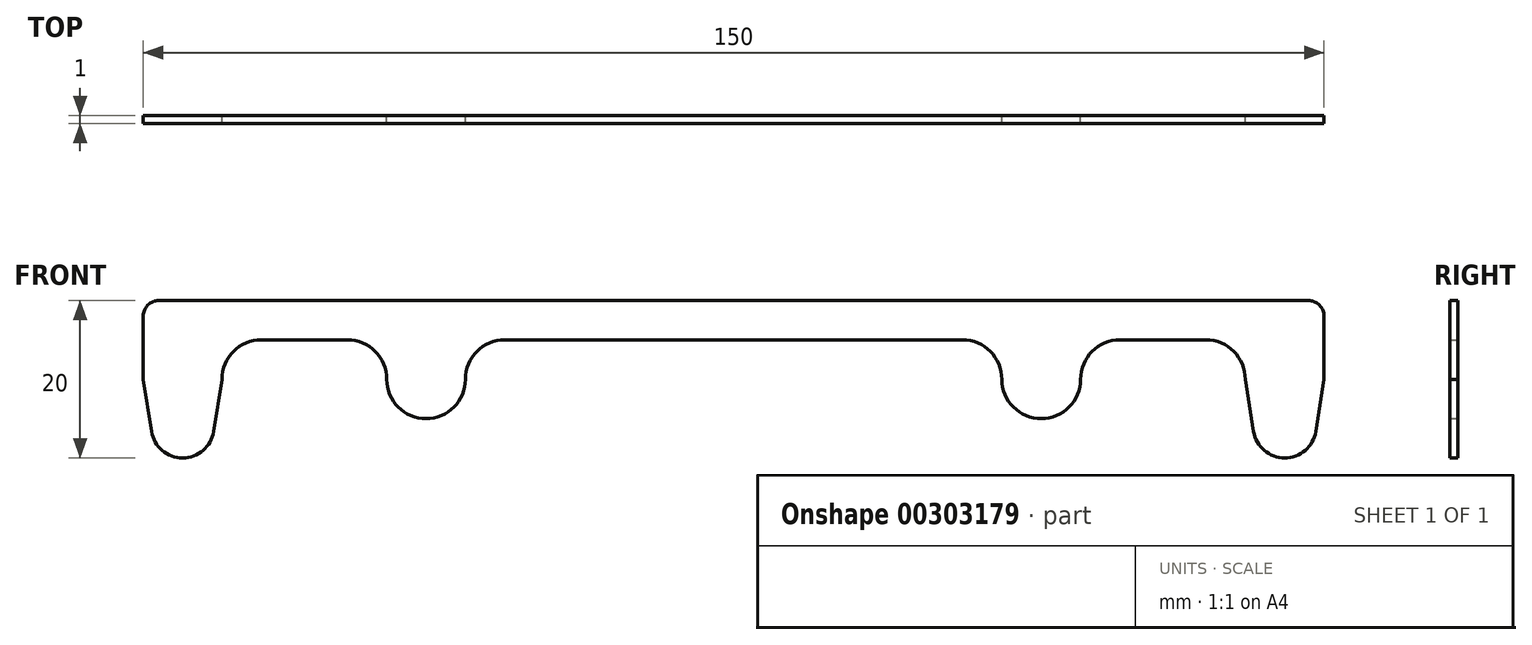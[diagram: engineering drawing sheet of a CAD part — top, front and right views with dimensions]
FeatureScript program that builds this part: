
annotation { "Feature Type Name" : "Feature", "Feature Type Description" : "" }
export const myFeature = defineFeature(function(context is Context, id is Id, definition is map)
    precondition{}
    {
        {
            var Q0;
            Q0=qCreatedBy(makeId("Front.planeOp"),FACE);
            var sketch = newSketch(context, id + "F0", { "sketchPlane" : qUnion([Q0])});
            skLineSegment(sketch, "E0.top", {"start": v(-28.13, 20.35) * mm, "end": v(29.87, 20.35) * mm});
            skLineSegment(sketch, "E0.left", {"start": v(-30.13, 10.35) * mm, "end": v(-30.13, 18.35) * mm});
            skLineSegment(sketch, "E1", {"start": v(27.87, 15.35) * mm, "end": v(15.8, 15.35) * mm});
            skLineSegment(sketch, "E2.top", {"start": v(-3.28, 5.35) * mm, "end": v(-3.28, 5.35) * mm});
            skLineSegment(sketch, "E2.left", {"start": v(-8.28, 10.35) * mm, "end": v(-8.28, 10.35) * mm});
            skLineSegment(sketch, "E2.right", {"start": v(1.72, 10.35) * mm, "end": v(1.72, 10.35) * mm});
            skLineSegment(sketch, "E3.trimOffspring", {"start": v(-13.28, 15.35) * mm, "end": v(-15.13, 15.35) * mm});
            skPoint(sketch, "E4.visualSharp", {"position": v(-20.13, 15.35) * mm});
            skArc(sketch, "E4.filletArc", {"start": v(-15.13, 15.35) * mm, "mid": v(-18.67, 13.89) * mm, "end": v(-20.13, 10.35) * mm});
            skPoint(sketch, "E5.visualSharp", {"position": v(-8.28, 15.35) * mm});
            skPoint(sketch, "E6.visualSharp", {"position": v(-8.28, 5.35) * mm});
            skPoint(sketch, "E7.visualSharp", {"position": v(1.72, 5.35) * mm});
            skPoint(sketch, "E8.visualSharp", {"position": v(1.72, 15.35) * mm});
            skPoint(sketch, "E9.visualSharp", {"position": v(-20.13, 0.35) * mm});
            skPoint(sketch, "E10.visualSharp", {"position": v(-30.13, 0.35) * mm});
            skPoint(sketch, "E11.visualSharp", {"position": v(-30.13, 20.35) * mm});
            skArc(sketch, "E11.filletArc", {"start": v(-28.13, 20.35) * mm, "mid": v(-29.54, 19.76) * mm, "end": v(-30.13, 18.35) * mm});
            skLineSegment(sketch, "E12", {"start": v(44.87, 39.66) * mm, "end": v(44.87, -4.16) * mm, "construction": true});
            skLineSegment(sketch, "E13.top", {"start": v(5.8, 5.35) * mm, "end": v(5.8, 5.35) * mm});
            skLineSegment(sketch, "E13.left", {"start": v(10.8, 10.35) * mm, "end": v(10.8, 10.35) * mm});
            skLineSegment(sketch, "E13.right", {"start": v(0.8, 10.35) * mm, "end": v(0.8, 10.35) * mm});
            skLineSegment(sketch, "E14", {"start": v(-13.28, 15.35) * mm, "end": v(-4.2, 15.35) * mm});
            skPoint(sketch, "E15.visualSharp", {"position": v(0.8, 15.35) * mm});
            skArc(sketch, "E15.filletArc", {"start": v(0.8, 10.35) * mm, "mid": v(-0.67, 13.89) * mm, "end": v(-4.2, 15.35) * mm});
            skPoint(sketch, "E16.newPointB", {"position": v(6.72, 15.35) * mm});
            skArc(sketch, "E16.filletArc", {"start": v(15.8, 15.35) * mm, "mid": v(12.26, 13.89) * mm, "end": v(10.8, 10.35) * mm});
            skPoint(sketch, "E17.visualSharp", {"position": v(10.8, 5.35) * mm});
            skArc(sketch, "E17.filletArc", {"start": v(5.8, 5.35) * mm, "mid": v(9.33, 6.81) * mm, "end": v(10.8, 10.35) * mm});
            skPoint(sketch, "E18.visualSharp", {"position": v(0.8, 5.35) * mm});
            skArc(sketch, "E18.filletArc", {"start": v(0.8, 10.35) * mm, "mid": v(2.26, 6.81) * mm, "end": v(5.8, 5.35) * mm});
            skLineSegment(sketch, "E19.MirrorCS", {"start": v(103.02, 15.35) * mm, "end": v(104.87, 15.35) * mm});
            skArc(sketch, "E20.MirrorCS", {"start": v(117.87, 20.35) * mm, "mid": v(119.28, 19.76) * mm, "end": v(119.87, 18.35) * mm});
            skArc(sketch, "E21.MirrorCS", {"start": v(88.94, 10.35) * mm, "mid": v(87.48, 6.81) * mm, "end": v(83.94, 5.35) * mm});
            skArc(sketch, "E22.MirrorCS", {"start": v(104.87, 15.35) * mm, "mid": v(108.4, 13.89) * mm, "end": v(109.87, 10.35) * mm});
            skLineSegment(sketch, "E23.MirrorCS", {"start": v(103.02, 15.35) * mm, "end": v(93.94, 15.35) * mm});
            skArc(sketch, "E24.MirrorCS", {"start": v(88.94, 10.35) * mm, "mid": v(90.4, 13.89) * mm, "end": v(93.94, 15.35) * mm});
            skArc(sketch, "E25.MirrorCS", {"start": v(83.94, 5.35) * mm, "mid": v(80.4, 6.81) * mm, "end": v(78.94, 10.35) * mm});
            skPoint(sketch, "E26.MirrorP", {"position": v(88.94, 5.35) * mm});
            skLineSegment(sketch, "E27.MirrorCS", {"start": v(117.87, 20.35) * mm, "end": v(59.87, 20.35) * mm});
            skLineSegment(sketch, "E28.MirrorCS", {"start": v(78.94, 10.35) * mm, "end": v(78.94, 10.35) * mm});
            skPoint(sketch, "E29.MirrorP", {"position": v(88.02, 15.35) * mm});
            skPoint(sketch, "E30.MirrorP", {"position": v(98.02, 15.35) * mm});
            skPoint(sketch, "E31.MirrorP", {"position": v(109.87, 15.35) * mm});
            skLineSegment(sketch, "E32.MirrorCS", {"start": v(93.02, 5.35) * mm, "end": v(93.02, 5.35) * mm});
            skLineSegment(sketch, "E33.MirrorCS", {"start": v(119.87, 10.35) * mm, "end": v(119.87, 18.35) * mm});
            skArc(sketch, "E34.MirrorCS", {"start": v(73.94, 15.35) * mm, "mid": v(77.48, 13.89) * mm, "end": v(78.94, 10.35) * mm});
            skLineSegment(sketch, "E35.MirrorCS", {"start": v(61.87, 15.35) * mm, "end": v(73.94, 15.35) * mm});
            skPoint(sketch, "E36.MirrorP", {"position": v(109.87, 0.35) * mm});
            skLineSegment(sketch, "E37.MirrorCS", {"start": v(88.02, 10.35) * mm, "end": v(88.02, 10.35) * mm});
            skPoint(sketch, "E38.MirrorP", {"position": v(98.02, 5.35) * mm});
            skLineSegment(sketch, "E39.MirrorCS", {"start": v(88.94, 10.35) * mm, "end": v(88.94, 10.35) * mm});
            skPoint(sketch, "E40.MirrorP", {"position": v(119.87, 20.35) * mm});
            skPoint(sketch, "E41.MirrorP", {"position": v(78.94, 5.35) * mm});
            skPoint(sketch, "E42.MirrorP", {"position": v(119.87, 0.35) * mm});
            skPoint(sketch, "E43.MirrorP", {"position": v(88.94, 15.35) * mm});
            skLineSegment(sketch, "E44.MirrorCS", {"start": v(98.02, 10.35) * mm, "end": v(98.02, 10.35) * mm});
            skPoint(sketch, "E45.MirrorP", {"position": v(88.02, 5.35) * mm});
            skLineSegment(sketch, "E46.MirrorCS", {"start": v(83.94, 5.35) * mm, "end": v(83.94, 5.35) * mm});
            skPoint(sketch, "E47.MirrorP", {"position": v(83.02, 15.35) * mm});
            skLineSegment(sketch, "E48", {"start": v(29.87, 20.35) * mm, "end": v(59.87, 20.35) * mm});
            skPoint(sketch, "E0.right.start.orphan", {"position": v(29.87, 17.35) * mm});
            skPoint(sketch, "E49.MirrorCS.end.orphan", {"position": v(59.87, 17.35) * mm});
            skLineSegment(sketch, "E50", {"start": v(27.87, 15.35) * mm, "end": v(61.87, 15.35) * mm});
            skArc(sketch, "E51", {"start": v(-29.08, 3.72) * mm, "mid": v(-25.13, 0.35) * mm, "end": v(-21.18, 3.72) * mm});
            skLineSegment(sketch, "E52", {"start": v(-20.13, 10.35) * mm, "end": v(-21.18, 3.72) * mm});
            skLineSegment(sketch, "E53", {"start": v(-25.13, 4.35) * mm, "end": v(-25.13, 18) * mm, "construction": true});
            skLineSegment(sketch, "E54.MirrorCS", {"start": v(-30.13, 10.35) * mm, "end": v(-29.08, 3.72) * mm});
            skPoint(sketch, "E9.filletArc.end.orphan", {"position": v(-20.13, 2.35) * mm});
            skPoint(sketch, "E55.orphan", {"position": v(-22.13, 0.35) * mm});
            skPoint(sketch, "E10.filletArc.end.orphan", {"position": v(-28.13, 0.35) * mm});
            skPoint(sketch, "E56.orphan", {"position": v(-30.13, 2.35) * mm});
            skPoint(sketch, "E57.MirrorCS.end.orphan", {"position": v(117.87, 0.35) * mm});
            skPoint(sketch, "E58.MirrorCS.end.orphan", {"position": v(109.87, 2.35) * mm});
            skPoint(sketch, "E58.MirrorCS.start.orphan", {"position": v(111.87, 0.35) * mm});
            skArc(sketch, "E59.MirrorCS", {"start": v(118.82, 3.72) * mm, "mid": v(114.87, 0.35) * mm, "end": v(110.92, 3.72) * mm});
            skLineSegment(sketch, "E60.MirrorCS", {"start": v(109.87, 10.35) * mm, "end": v(110.92, 3.72) * mm});
            skLineSegment(sketch, "E61.MirrorCS", {"start": v(119.87, 10.35) * mm, "end": v(118.82, 3.72) * mm});
            skPoint(sketch, "E62.orphan", {"position": v(119.87, 2.35) * mm});
            skSolve(sketch);
        }
        {
            var Q0;
            Q0 = qSketchRegion(id + "F0", true);
            var Q1;
            Q1 = qConstructionFilter(qBodyType(qCreatedBy(id + "F0" ,EDGE), BodyType.WIRE), ConstructionObject.NO);
            extrude(context, id + "F1", {"entities" : qUnion([Q0]), "surfaceEntities" : qUnion([Q1]), "depth" : 1 * mm});
        }
    });
